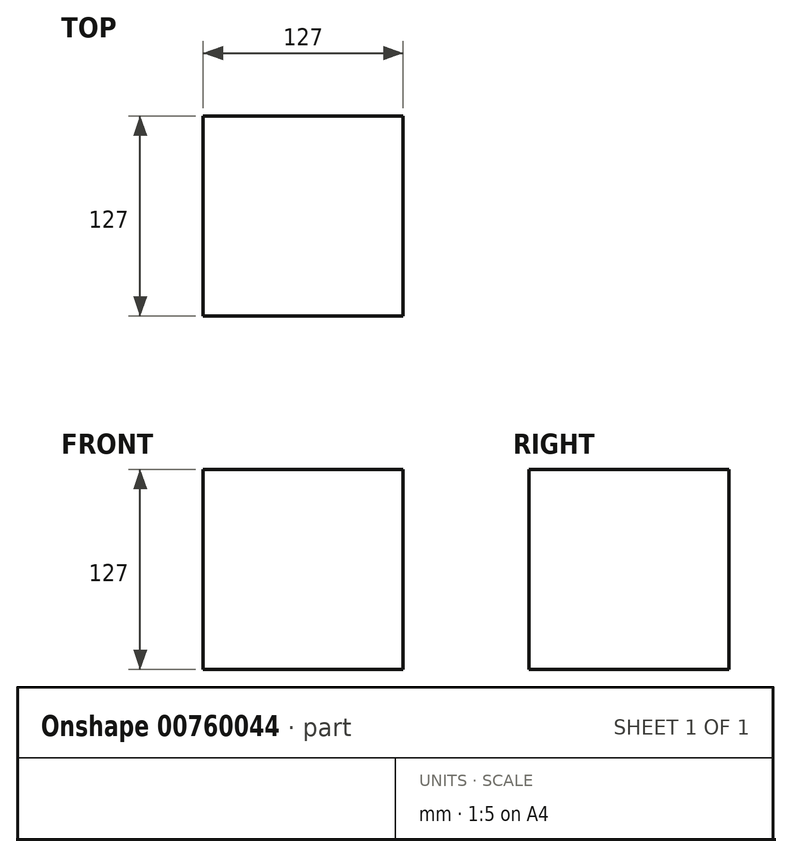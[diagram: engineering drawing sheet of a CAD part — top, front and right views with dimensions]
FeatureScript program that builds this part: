
annotation { "Feature Type Name" : "Feature", "Feature Type Description" : "" }
export const myFeature = defineFeature(function(context is Context, id is Id, definition is map)
    precondition{}
    {
        {
            var Q0;
            Q0=qCreatedBy(makeId("Front.planeOp"),FACE);
            var sketch = newSketch(context, id + "F0", { "sketchPlane" : qUnion([Q0])});
            skLineSegment(sketch, "E0.bottom", {"start": v(0, 0) * mm, "end": v(-127, 0) * mm});
            skLineSegment(sketch, "E0.top", {"start": v(0, 127) * mm, "end": v(-127, 127) * mm});
            skLineSegment(sketch, "E0.left", {"start": v(0, 0) * mm, "end": v(0, 127) * mm});
            skLineSegment(sketch, "E0.right", {"start": v(-127, 0) * mm, "end": v(-127, 127) * mm});
            skSolve(sketch);
        }
        {
            var Q0;
            Q0 = qSketchRegion(id + "F0", true);
            extrude(context, id + "F1", {"entities" : qUnion([Q0]), "depth" : 127 * mm, "offsetDistance" : 25.4 * mm});
        }
    });
